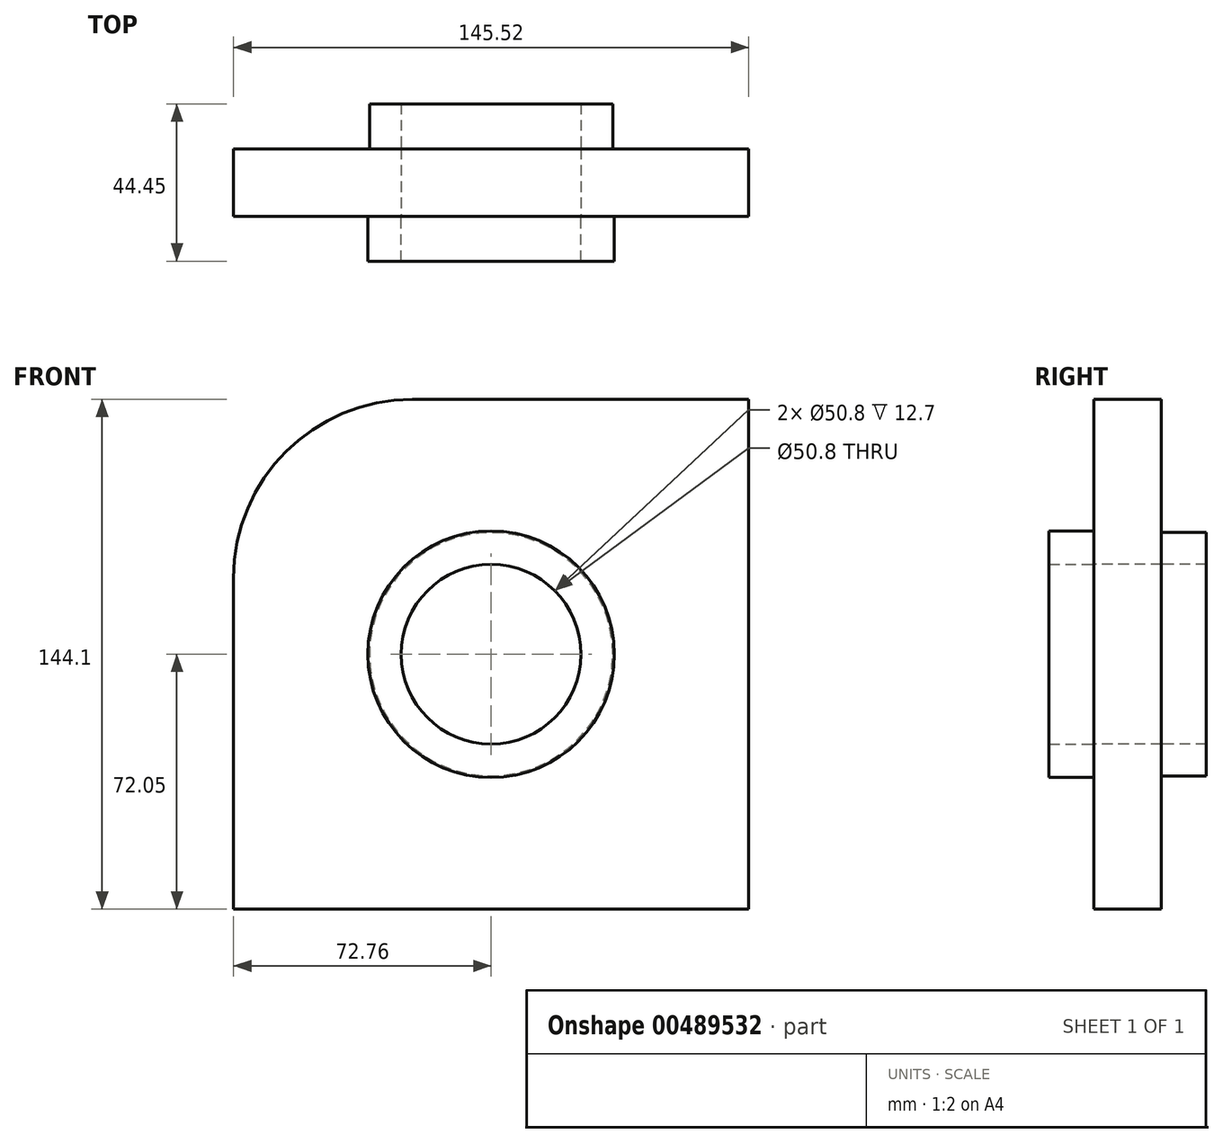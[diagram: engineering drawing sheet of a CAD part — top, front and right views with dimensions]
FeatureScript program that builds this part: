
annotation { "Feature Type Name" : "Feature", "Feature Type Description" : "" }
export const myFeature = defineFeature(function(context is Context, id is Id, definition is map)
    precondition{}
    {
        {
            var Q0;
            Q0=qCreatedBy(makeId("Front.planeOp"),FACE);
            var sketch = newSketch(context, id + "F0", { "sketchPlane" : qUnion([Q0])});
            skLineSegment(sketch, "E0.bottom", {"start": v(-22.23, 72.05) * mm, "end": v(72.76, 72.05) * mm});
            skLineSegment(sketch, "E0.top", {"start": v(-72.76, -72.05) * mm, "end": v(72.76, -72.05) * mm});
            skLineSegment(sketch, "E0.left", {"start": v(-72.76, 21.53) * mm, "end": v(-72.76, -72.05) * mm});
            skLineSegment(sketch, "E0.right", {"start": v(72.76, 72.05) * mm, "end": v(72.76, -72.05) * mm});
            skPoint(sketch, "E0.middle", {"position": v(0, 0) * mm});
            skPoint(sketch, "E1.visualSharp", {"position": v(-72.76, 72.05) * mm});
            skArc(sketch, "E1.filletArc", {"start": v(-22.23, 72.05) * mm, "mid": v(-57.96, 57.25) * mm, "end": v(-72.76, 21.53) * mm});
            skSolve(sketch);
        }
        {
            var Q0;
            Q0=makeQuery(id+"F0.imprint","IMPRINT",FACE,{"disambiguationData":[TD([[makeQuery(id+"F0.imprint","IMPRINT",EDGE,{"derivedFrom":sQuery(id+"F0.wireOp",EDGE,"E0.bottom")}),-1.0]])]});
            extrude(context, id + "F1", {"entities" : qUnion([Q0]), "depth" : 19.05 * mm});
        }
        {
            var Q0;
            Q0=makeQuery(id+"F1.opExtrude","CAP_FACE",FACE,{"disambiguationData":[OSD([sQuery(id+"F0.wireOp",EDGE,"E0.bottom"),sQuery(id+"F0.wireOp",EDGE,"E0.top"),sQuery(id+"F0.wireOp",EDGE,"E0.left"),sQuery(id+"F0.wireOp",EDGE,"E0.right")])],"isStart":false});
            var sketch = newSketch(context, id + "F2", { "sketchPlane" : qUnion([Q0])});
            skCircle(sketch, "E2", {"center": v(0, 0) * mm, "radius": 25.4 * mm});
            skSolve(sketch);
        }
        {
            var Q0;
            Q0=makeQuery(id+"F2.imprint","IMPRINT",FACE,{"disambiguationData":[TD([[makeQuery(id+"F2.imprint","IMPRINT",EDGE,{"derivedFrom":sQuery(id+"F2.wireOp",EDGE,"E2")}),1.0]])]});
            extrude(context, id + "F3", {"entities" : qUnion([Q0]), "operationType" : NewBodyOperationType.REMOVE, "endBound" : BoundingType.THROUGH_ALL, "oppositeDirection" : true, "depth" : 25.4 * mm});
        }
        {
            var Q0;
            Q0=makeQuery(id+"F1.opExtrude","CAP_FACE",FACE,{"disambiguationData":[OSD([sQuery(id+"F0.wireOp",EDGE,"E0.bottom"),sQuery(id+"F0.wireOp",EDGE,"E0.top"),sQuery(id+"F0.wireOp",EDGE,"E0.left"),sQuery(id+"F0.wireOp",EDGE,"E0.right"),sQuery(id+"F0.wireOp",EDGE,"E1.filletArc")])],"isStart":false});
            var sketch = newSketch(context, id + "F4", { "sketchPlane" : qUnion([Q0])});
            skCircle(sketch, "E3", {"center": v(0, 0) * mm, "radius": 34.82 * mm});
            skSolve(sketch);
        }
        {
            var Q0;
            Q0=makeQuery(id+"F4.imprint","IMPRINT",FACE,{"disambiguationData":[TD([[makeQuery(id+"F4.imprint","IMPRINT",EDGE,{"derivedFrom":sQuery(id+"F4.wireOp",EDGE,"E3")}),1.0]])]});
            var Q1;
            Q1=sQuery(id+"F4.wireOp",EDGE,"E3");
            extrude(context, id + "F5", {"entities" : qUnion([Q0]), "surfaceEntities" : qUnion([Q1]), "depth" : 12.7 * mm});
        }
        {
            var Q0;
            Q0=qCreatedBy(makeId("Front.planeOp"),FACE);
            var sketch = newSketch(context, id + "F6", { "sketchPlane" : qUnion([Q0])});
            skCircle(sketch, "E4", {"center": v(0, 0) * mm, "radius": 34.37 * mm});
            skCircle(sketch, "E5.0", {"center": v(0, 0) * mm, "radius": 25.4 * mm});
            skSolve(sketch);
        }
        {
            var Q0;
            Q0=makeQuery(id+"F6.imprint","IMPRINT",FACE,{"disambiguationData":[TD([[makeQuery(id+"F6.imprint","IMPRINT",EDGE,{"derivedFrom":sQuery(id+"F6.wireOp",EDGE,"E4")}),1.0]])]});
            var Q1;
            Q1=sQuery(id+"F6.wireOp",EDGE,"E4");
            extrude(context, id + "F7", {"entities" : qUnion([Q0]), "surfaceEntities" : qUnion([Q1]), "oppositeDirection" : true, "depth" : 12.7 * mm});
        }
    });
